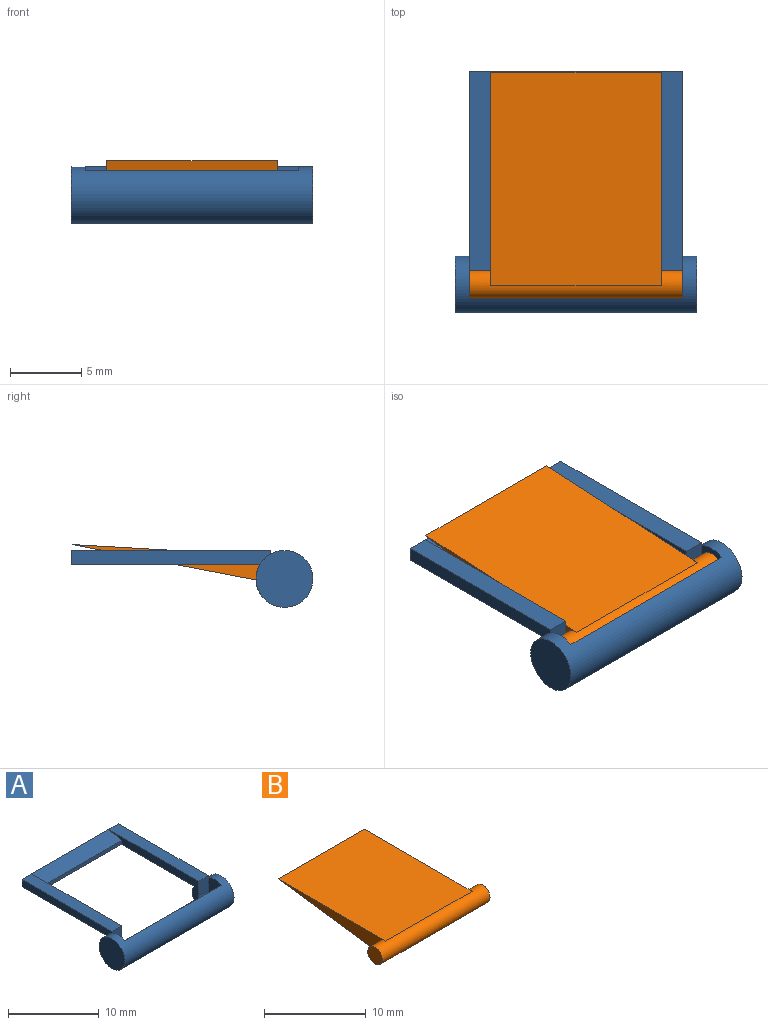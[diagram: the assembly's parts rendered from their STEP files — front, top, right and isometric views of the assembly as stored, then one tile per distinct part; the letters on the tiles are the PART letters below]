
ASSEMBLY  parts=2 mates=1
PART A: 20 faces, bbox 17x17x4 mm
  f0: plane 12x2mm, normal (0,-0.24,0.97), area 24.7mm2, adj f1,f3,f9,f17
  f1: plane 12x0.5mm, normal (0,-1,0), area 6mm2, adj f0,f2,f9,f17
  f2: plane 15x13.27mm, normal (0,0,-1), area 63.8mm2, adj f1,f3,f4,f7,f9,f14,f17
  f3: plane 15x1mm, normal (0,1,0), area 15mm2, adj f0,f2,f4,f8,f14,f16
  f4: plane 14x1mm, normal (1,0,0), area 13.7mm2, adj f2,f3,f5,f7,f8
  f5: plane 2x1.5mm, normal (0,-1,0), area 3mm2, adj f4,f6,f8,f9,f12
  f6: cylinder r=1mm len=15mm, axis (1,0,0), area 28.3mm2, adj f5,f9,f10,f12,f13,f15,f17,f19
  f7: cylinder r=2mm len=17mm, axis (1,0,0), area 141.4mm2, adj f2,f4,f9,f10,f11,f12,f13,f14
  f8: plane 14x1.5mm, normal (0,0,1), area 21mm2, adj f3,f4,f5,f9
  f9: plane 15x3mm, normal (-1,0,0), area 14.5mm2, adj f0,f1,f2,f5,f6,f7,f8,f10
  f10: plane 12x1.73mm, normal (0,0,1), area 20.8mm2, adj f6,f7,f9,f17
  f11: plane 4x4mm, normal (1,0,0), area 12.6mm2, adj f7
  f12: plane 3x2mm, normal (-1,0,0), area 5.4mm2, adj f5,f6,f7,f13
  f13: plane 15x1.73mm, normal (0,1,0), area 26mm2, adj f6,f7,f12,f19
  f14: plane 14x1mm, normal (-1,0,0), area 13.7mm2, adj f2,f3,f7,f15,f16
  f15: plane 2x1.5mm, normal (0,-1,0), area 3mm2, adj f6,f14,f16,f17,f19
  f16: plane 14x1.5mm, normal (0,0,1), area 21mm2, adj f3,f14,f15,f17
  f17: plane 15x3mm, normal (1,0,0), area 14.5mm2, adj f0,f1,f2,f6,f7,f10,f15,f16
  f18: plane 4x4mm, normal (-1,0,0), area 12.6mm2, adj f7
  f19: plane 3x2mm, normal (1,0,0), area 5.4mm2, adj f6,f7,f13,f15
PART B: 7 faces, bbox 15x16x2 mm
  f0: plane 15x12mm, normal (0,0,1), area 180mm2, adj f1,f2,f3,f4
  f1: plane 15x15mm, normal (0,0.13,-0.99), area 182.4mm2, adj f0,f2,f3,f4,f5,f6
  f2: plane 15x1.97mm, normal (1,0,0), area 13.4mm2, adj f0,f1,f4
  f3: plane 15x1.97mm, normal (-1,0,0), area 13.4mm2, adj f0,f1,f4
  f4: cylinder r=1mm len=15mm, axis (-1,0,0), area 55.8mm2, adj f0,f1,f2,f3,f5,f6
  f5: plane 2x2mm, normal (1,0,0), area 3.1mm2, adj f1,f4
  f6: plane 2x2mm, normal (-1,0,0), area 3.1mm2, adj f1,f4
PLACE A t=(-0.26,-5.12,5.04)mm fixed
PLACE B rot(axis=(1,0,0),3.3deg) t=(-7.76,-5.12,5.6)mm
MATE revolute B.f4 <-> A.f19  axis (-1,0,0) through (-15.26,-5.12,5.6)mm
